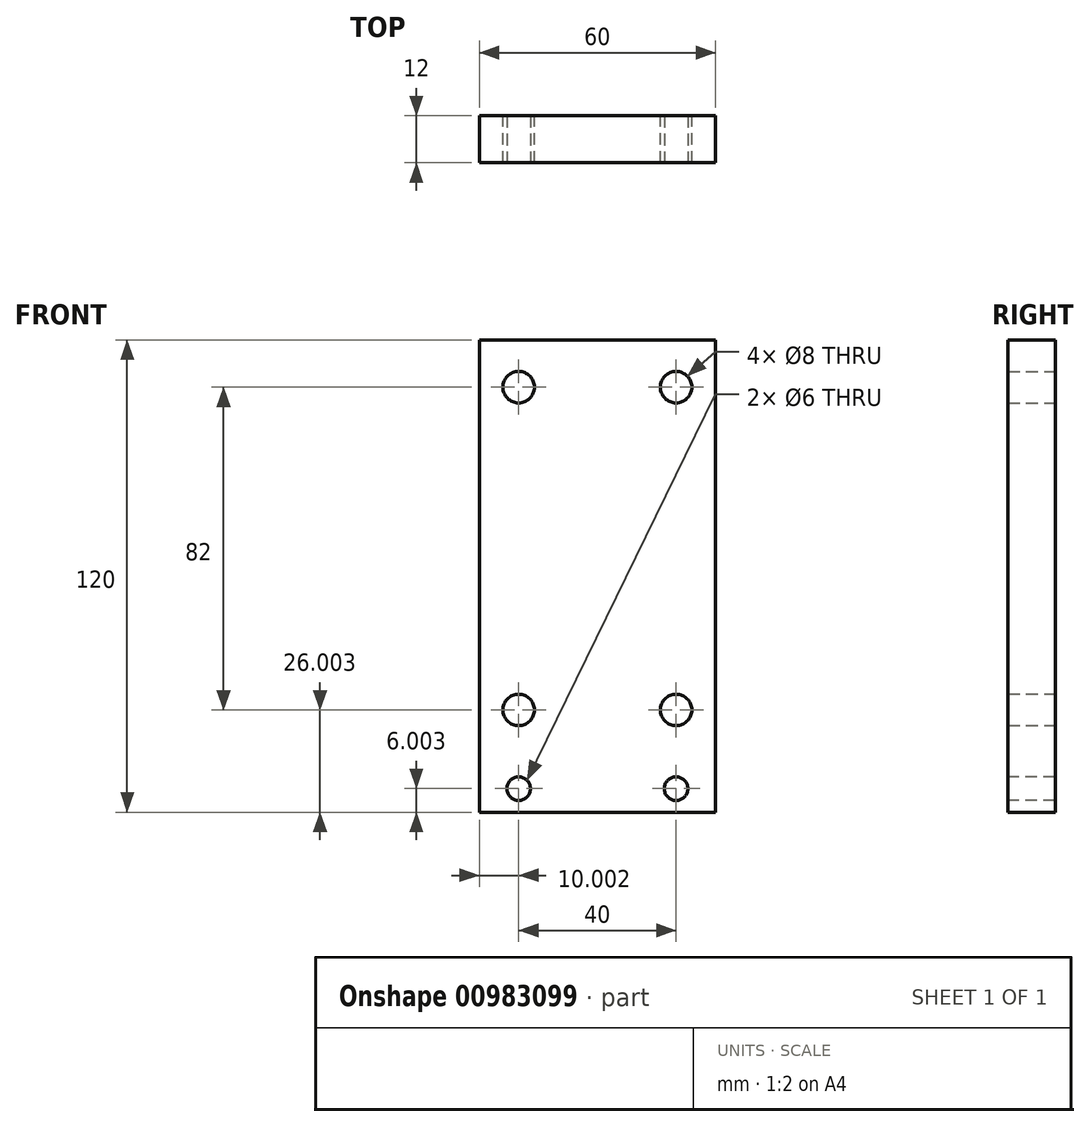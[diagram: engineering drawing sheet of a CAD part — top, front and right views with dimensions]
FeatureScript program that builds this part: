
annotation { "Feature Type Name" : "Feature", "Feature Type Description" : "" }
export const myFeature = defineFeature(function(context is Context, id is Id, definition is map)
    precondition{}
    {
        {
            var Q0;
            Q0=qCreatedBy(makeId("Front.planeOp"),FACE);
            var sketch = newSketch(context, id + "F0", { "sketchPlane" : qUnion([Q0])});
            skLineSegment(sketch, "E0.bottom", {"start": v(-30.33, 80.63) * mm, "end": v(29.67, 80.63) * mm});
            skLineSegment(sketch, "E0.top", {"start": v(-30.33, -39.37) * mm, "end": v(29.67, -39.37) * mm});
            skLineSegment(sketch, "E0.left", {"start": v(-30.33, 80.63) * mm, "end": v(-30.33, -39.37) * mm});
            skLineSegment(sketch, "E0.right", {"start": v(29.67, 80.63) * mm, "end": v(29.67, -39.37) * mm});
            skCircle(sketch, "E1", {"center": v(-20.33, 68.63) * mm, "radius": 4 * mm});
            skCircle(sketch, "E2", {"center": v(19.67, 68.63) * mm, "radius": 4 * mm});
            skCircle(sketch, "E3", {"center": v(-20.33, -13.37) * mm, "radius": 4 * mm});
            skCircle(sketch, "E4", {"center": v(19.67, -13.37) * mm, "radius": 4 * mm});
            skSolve(sketch);
        }
        {
            var Q0;
            Q0=qSketchRegion(id+"F0",true);
            extrude(context, id + "F1", {"entities" : qUnion([Q0]), "depth" : 12 * mm, "offsetDistance" : 25 * mm});
        }
        {
            var Q0;
            Q0=makeQuery(id+"F1.opExtrude","CAP_FACE",FACE,{"disambiguationData":[OSD([sQuery(id+"F0.wireOp",EDGE,"E0.bottom"),sQuery(id+"F0.wireOp",EDGE,"E0.top"),sQuery(id+"F0.wireOp",EDGE,"E0.left"),sQuery(id+"F0.wireOp",EDGE,"E0.right"),sQuery(id+"F0.wireOp",EDGE,"E1"),sQuery(id+"F0.wireOp",EDGE,"E2"),sQuery(id+"F0.wireOp",EDGE,"E3"),sQuery(id+"F0.wireOp",EDGE,"E4")])],"isStart":false});
            var sketch = newSketch(context, id + "F2", { "sketchPlane" : qUnion([Q0])});
            skCircle(sketch, "E5", {"center": v(-20.33, -33.37) * mm, "radius": 3 * mm});
            skCircle(sketch, "E6", {"center": v(19.67, -33.37) * mm, "radius": 3 * mm});
            skSolve(sketch);
        }
        {
            var Q0;
            Q0=sQuery(id+"F2.wireOp",VERTEX,"E5.center");
            var Q1;
            Q1=sQuery(id+"F2.wireOp",VERTEX,"E6.center");
            var Q2;
            Q2=makeQuery(id+"F1.opExtrude","SWEPT_BODY",BODY,{"disambiguationData":[OSD([sQuery(id+"F0.wireOp",EDGE,"E0.bottom"),sQuery(id+"F0.wireOp",EDGE,"E0.top"),sQuery(id+"F0.wireOp",EDGE,"E0.left"),sQuery(id+"F0.wireOp",EDGE,"E0.right"),sQuery(id+"F0.wireOp",EDGE,"E1"),sQuery(id+"F0.wireOp",EDGE,"E2"),sQuery(id+"F0.wireOp",EDGE,"E3"),sQuery(id+"F0.wireOp",EDGE,"E4")])]});
            hole(context, id + "F3", {"style" : HoleStyle.SIMPLE, "endStyle" : HoleEndStyle.THROUGH, "holeDiameter" : 6 * mm, "majorDiameter" : 5 * mm, "isTappedThrough" : true, "tappedDepth" : 12 * mm, "tapClearance" : 3, "locations" : qUnion([Q0, Q1]), "scope" : qUnion([Q2])});
        }
    });
